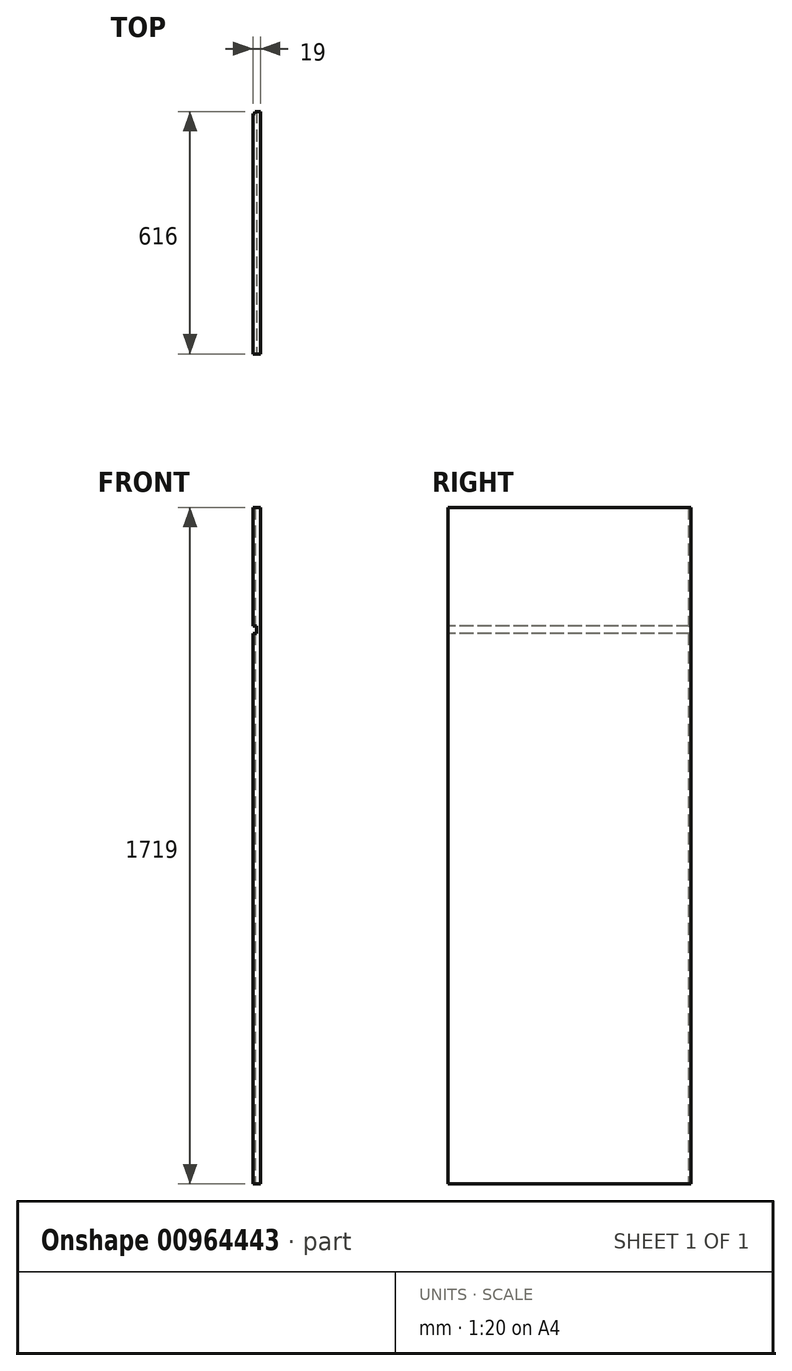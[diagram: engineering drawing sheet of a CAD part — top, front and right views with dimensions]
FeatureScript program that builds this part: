
annotation { "Feature Type Name" : "Feature", "Feature Type Description" : "" }
export const myFeature = defineFeature(function(context is Context, id is Id, definition is map)
    precondition{}
    {
        {
            var Q0;
            Q0=qCreatedBy(makeId("Right.planeOp"),FACE);
            var sketch = newSketch(context, id + "F0", { "sketchPlane" : qUnion([Q0])});
            skLineSegment(sketch, "E0.bottom", {"start": v(0, 0) * mm, "end": v(616, 0) * mm});
            skLineSegment(sketch, "E0.top", {"start": v(0, 1719) * mm, "end": v(616, 1719) * mm});
            skLineSegment(sketch, "E0.left", {"start": v(0, 0) * mm, "end": v(0, 1719) * mm});
            skLineSegment(sketch, "E0.right", {"start": v(616, 0) * mm, "end": v(616, 1719) * mm});
            skSolve(sketch);
        }
        {
            var Q0;
            Q0=makeQuery(id+"F0.imprint","IMPRINT",FACE,{"disambiguationData":[TD([[makeQuery(id+"F0.imprint","IMPRINT",EDGE,{"derivedFrom":sQuery(id+"F0.wireOp",EDGE,"E0.bottom")}),1.0]])]});
            extrude(context, id + "F1", {"entities" : qUnion([Q0]), "oppositeDirection" : true, "depth" : 19 * mm, "offsetDistance" : 25 * mm});
        }
        {
            var Q0;
            Q0=qCreatedBy(makeId("Top.planeOp"),FACE);
            var sketch = newSketch(context, id + "F2", { "sketchPlane" : qUnion([Q0])});
            skLineSegment(sketch, "E1.bottom", {"start": v(-19, 616) * mm, "end": v(-13, 616) * mm});
            skLineSegment(sketch, "E1.top", {"start": v(-19, 610) * mm, "end": v(-13, 610) * mm});
            skLineSegment(sketch, "E1.left", {"start": v(-19, 616) * mm, "end": v(-19, 610) * mm});
            skLineSegment(sketch, "E1.right", {"start": v(-13, 616) * mm, "end": v(-13, 610) * mm});
            skSolve(sketch);
        }
        {
            var Q0;
            Q0 = qSketchRegion(id + "F2", true);
            extrude(context, id + "F3", {"entities" : qUnion([Q0]), "operationType" : NewBodyOperationType.REMOVE, "endBound" : BoundingType.THROUGH_ALL, "depth" : 25 * mm, "offsetDistance" : 25 * mm});
        }
        {
            var Q0;
            Q0=qCreatedBy(makeId("Front.planeOp"),FACE);
            var sketch = newSketch(context, id + "F4", { "sketchPlane" : qUnion([Q0])});
            skLineSegment(sketch, "E2.bottom", {"start": v(-19, 1418) * mm, "end": v(-10, 1418) * mm});
            skLineSegment(sketch, "E2.top", {"start": v(-19, 1399) * mm, "end": v(-10, 1399) * mm});
            skLineSegment(sketch, "E2.left", {"start": v(-19, 1418) * mm, "end": v(-19, 1399) * mm});
            skLineSegment(sketch, "E2.right", {"start": v(-10, 1418) * mm, "end": v(-10, 1399) * mm});
            skSolve(sketch);
        }
        {
            var Q0;
            Q0 = qSketchRegion(id + "F4", true);
            extrude(context, id + "F5", {"entities" : qUnion([Q0]), "operationType" : NewBodyOperationType.REMOVE, "endBound" : BoundingType.THROUGH_ALL, "oppositeDirection" : true, "depth" : 25 * mm, "offsetDistance" : 25 * mm});
        }
    });
